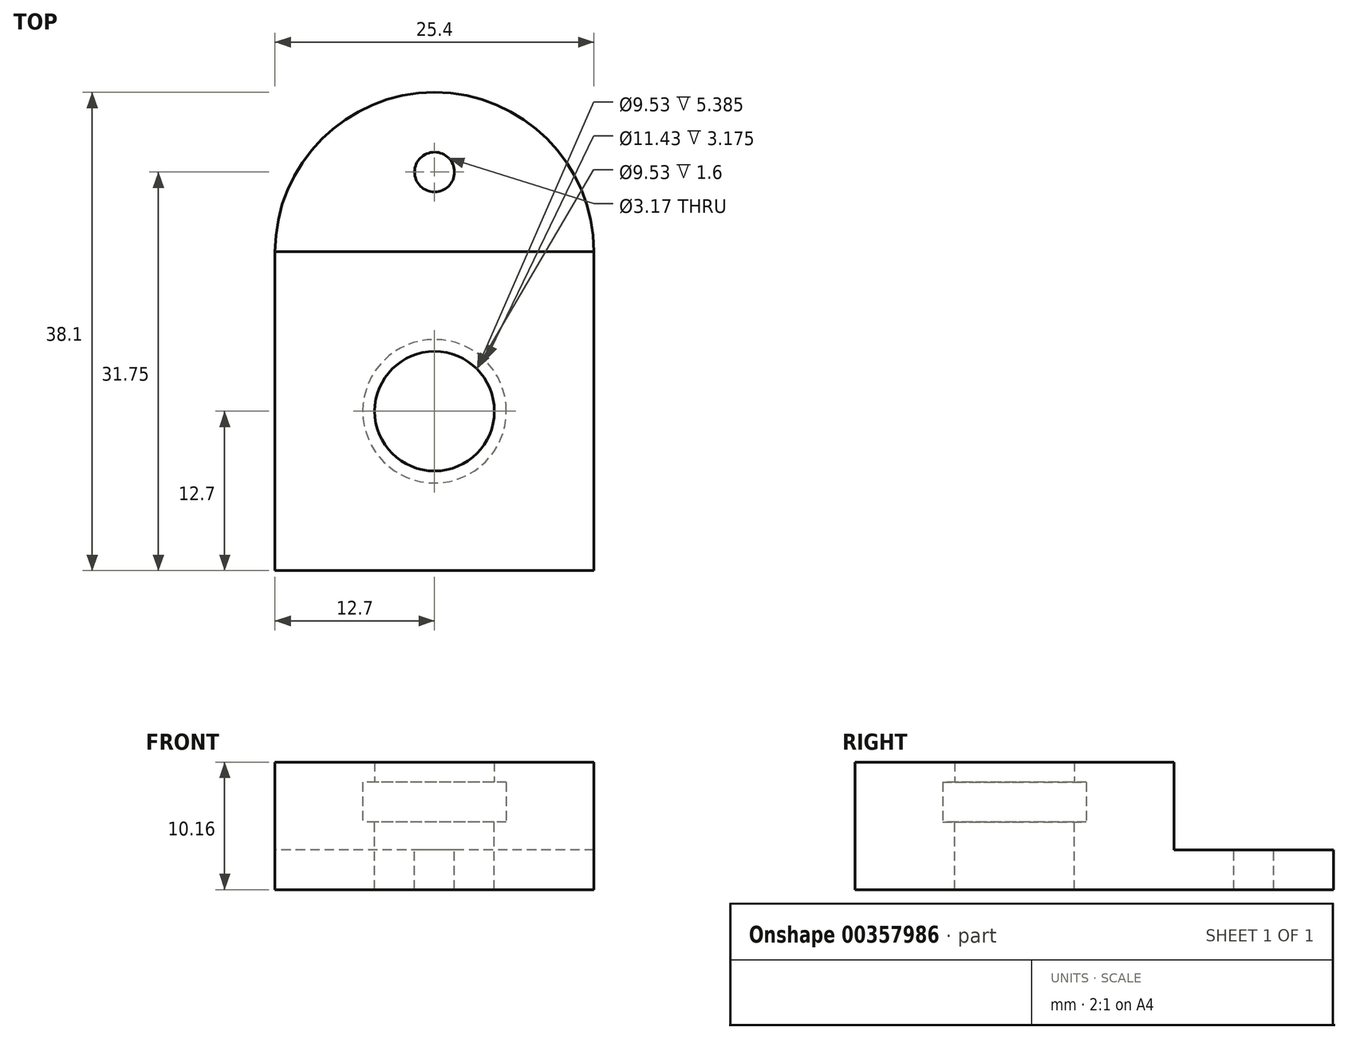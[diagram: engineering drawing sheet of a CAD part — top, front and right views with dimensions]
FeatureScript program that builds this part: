
annotation { "Feature Type Name" : "Feature", "Feature Type Description" : "" }
export const myFeature = defineFeature(function(context is Context, id is Id, definition is map)
    precondition{}
    {
        {
            var Q0;
            Q0=qCreatedBy(makeId("Top.planeOp"),FACE);
            var sketch = newSketch(context, id + "F0", { "sketchPlane" : qUnion([Q0])});
            skLineSegment(sketch, "E0.top", {"start": v(12.7, -12.7) * mm, "end": v(-12.7, -12.7) * mm});
            skLineSegment(sketch, "E0.left", {"start": v(12.7, 12.7) * mm, "end": v(12.7, -12.7) * mm});
            skLineSegment(sketch, "E0.right", {"start": v(-12.7, 12.7) * mm, "end": v(-12.7, -12.7) * mm});
            skPoint(sketch, "E0.middle", {"position": v(0, 0) * mm});
            skArc(sketch, "E1", {"start": v(-12.7, 12.7) * mm, "mid": v(0, 25.4) * mm, "end": v(12.7, 12.7) * mm});
            skSolve(sketch);
        }
        {
            var Q0;
            Q0=makeQuery(id+"F0.imprint","IMPRINT",FACE,{"disambiguationData":[TD([[makeQuery(id+"F0.imprint","IMPRINT",EDGE,{"derivedFrom":sQuery(id+"F0.wireOp",EDGE,"E0.top")}),-1.0]])]});
            extrude(context, id + "F1", {"entities" : qUnion([Q0]), "depth" : 3.17 * mm});
        }
        {
            var Q0;
            Q0=makeQuery(id+"F1.opExtrude","CAP_FACE",FACE,{"disambiguationData":[OSD([sQuery(id+"F0.wireOp",EDGE,"E0.top"),sQuery(id+"F0.wireOp",EDGE,"E0.left"),sQuery(id+"F0.wireOp",EDGE,"E0.right"),sQuery(id+"F0.wireOp",EDGE,"E1")])],"isStart":false});
            var sketch = newSketch(context, id + "F2", { "sketchPlane" : qUnion([Q0])});
            skLineSegment(sketch, "E2.bottom", {"start": v(12.7, 12.7) * mm, "end": v(-12.7, 12.7) * mm});
            skLineSegment(sketch, "E2.top", {"start": v(12.7, -12.7) * mm, "end": v(-12.7, -12.7) * mm});
            skLineSegment(sketch, "E2.left", {"start": v(12.7, 12.7) * mm, "end": v(12.7, -12.7) * mm});
            skLineSegment(sketch, "E2.right", {"start": v(-12.7, 12.7) * mm, "end": v(-12.7, -12.7) * mm});
            skPoint(sketch, "E2.middle", {"position": v(0, 0) * mm});
            skSolve(sketch);
        }
        {
            var Q0;
            Q0 = qSketchRegion(id + "F2", true);
            extrude(context, id + "F3", {"entities" : qUnion([Q0]), "operationType" : NewBodyOperationType.ADD, "depth" : 2.2 * mm});
        }
        {
            var Q0;
            Q0=makeQuery(id+"F3.opExtrude","CAP_FACE",FACE,{"disambiguationData":[OSD([sQuery(id+"F2.wireOp",EDGE,"E2.bottom"),sQuery(id+"F2.wireOp",EDGE,"E2.top"),sQuery(id+"F2.wireOp",EDGE,"E2.left"),sQuery(id+"F2.wireOp",EDGE,"E2.right")])],"isStart":false});
            var sketch = newSketch(context, id + "F4", { "sketchPlane" : qUnion([Q0])});
            skCircle(sketch, "E3", {"center": v(0, 0) * mm, "radius": 4.76 * mm});
            skSolve(sketch);
        }
        {
            var Q0;
            Q0=sQuery(id+"F4.wireOp",VERTEX,"E3.center");
            var Q1;
            Q1=makeQuery(id+"F1.opExtrude","SWEPT_BODY",BODY,{"disambiguationData":[OSD([sQuery(id+"F0.wireOp",EDGE,"E0.top"),sQuery(id+"F0.wireOp",EDGE,"E0.left"),sQuery(id+"F0.wireOp",EDGE,"E0.right"),sQuery(id+"F0.wireOp",EDGE,"E1")])]});
            hole(context, id + "F5", {"style" : HoleStyle.SIMPLE, "endStyle" : HoleEndStyle.THROUGH, "holeDiameter" : 9.52 * mm, "isTappedThrough" : true, "tappedDepth" : 12.7 * mm, "tapClearance" : 3, "locations" : qUnion([Q0]), "scope" : qUnion([Q1])});
        }
        {
            var Q0;
            Q0=makeQuery(id+"F3.opExtrude","CAP_FACE",FACE,{"disambiguationData":[OSD([sQuery(id+"F2.wireOp",EDGE,"E2.bottom"),sQuery(id+"F2.wireOp",EDGE,"E2.top"),sQuery(id+"F2.wireOp",EDGE,"E2.left"),sQuery(id+"F2.wireOp",EDGE,"E2.right")])],"isStart":false});
            var sketch = newSketch(context, id + "F6", { "sketchPlane" : qUnion([Q0])});
            skLineSegment(sketch, "E4.bottom", {"start": v(12.7, 12.7) * mm, "end": v(-12.7, 12.7) * mm});
            skLineSegment(sketch, "E4.top", {"start": v(12.7, -12.7) * mm, "end": v(-12.7, -12.7) * mm});
            skLineSegment(sketch, "E4.left", {"start": v(12.7, 12.7) * mm, "end": v(12.7, -12.7) * mm});
            skLineSegment(sketch, "E4.right", {"start": v(-12.7, 12.7) * mm, "end": v(-12.7, -12.7) * mm});
            skPoint(sketch, "E4.middle", {"position": v(0, 0) * mm});
            skCircle(sketch, "E5", {"center": v(0, 0) * mm, "radius": 5.72 * mm});
            skSolve(sketch);
        }
        {
            var Q0;
            Q0 = qSketchRegion(id + "F6", true);
            extrude(context, id + "F7", {"entities" : qUnion([Q0]), "operationType" : NewBodyOperationType.ADD, "depth" : 3.17 * mm});
        }
        {
            var Q0;
            Q0=makeQuery(id+"F7.opExtrude","CAP_FACE",FACE,{"disambiguationData":[OSD([sQuery(id+"F6.wireOp",EDGE,"E4.bottom"),sQuery(id+"F6.wireOp",EDGE,"E4.top"),sQuery(id+"F6.wireOp",EDGE,"E4.left"),sQuery(id+"F6.wireOp",EDGE,"E4.right"),sQuery(id+"F6.wireOp",EDGE,"E5")])],"isStart":false});
            var sketch = newSketch(context, id + "F8", { "sketchPlane" : qUnion([Q0])});
            skLineSegment(sketch, "E6.bottom", {"start": v(12.7, 12.7) * mm, "end": v(-12.7, 12.7) * mm});
            skLineSegment(sketch, "E6.top", {"start": v(12.7, -12.7) * mm, "end": v(-12.7, -12.7) * mm});
            skLineSegment(sketch, "E6.left", {"start": v(12.7, 12.7) * mm, "end": v(12.7, -12.7) * mm});
            skLineSegment(sketch, "E6.right", {"start": v(-12.7, 12.7) * mm, "end": v(-12.7, -12.7) * mm});
            skPoint(sketch, "E6.middle", {"position": v(0, 0) * mm});
            skCircle(sketch, "E7", {"center": v(0, 0) * mm, "radius": 4.76 * mm});
            skSolve(sketch);
        }
        {
            var Q0;
            Q0 = qSketchRegion(id + "F8", true);
            extrude(context, id + "F9", {"entities" : qUnion([Q0]), "operationType" : NewBodyOperationType.ADD, "depth" : 1.6 * mm});
        }
        {
            var Q0;
            Q0=makeQuery(id+"F1.opExtrude","CAP_FACE",FACE,{"disambiguationData":[OSD([sQuery(id+"F0.wireOp",EDGE,"E0.top"),sQuery(id+"F0.wireOp",EDGE,"E0.left"),sQuery(id+"F0.wireOp",EDGE,"E0.right"),sQuery(id+"F0.wireOp",EDGE,"E1")])],"isStart":false});
            var sketch = newSketch(context, id + "F10", { "sketchPlane" : qUnion([Q0])});
            skPoint(sketch, "E8", {"position": v(0, 19.05) * mm});
            skSolve(sketch);
        }
        {
            var Q0;
            Q0=sQuery(id+"F10.wireOp",VERTEX,"E8");
            var Q1;
            Q1=makeQuery(id+"F1.opExtrude","SWEPT_BODY",BODY,{"disambiguationData":[OSD([sQuery(id+"F0.wireOp",EDGE,"E0.top"),sQuery(id+"F0.wireOp",EDGE,"E0.left"),sQuery(id+"F0.wireOp",EDGE,"E0.right"),sQuery(id+"F0.wireOp",EDGE,"E1")])]});
            hole(context, id + "F11", {"style" : HoleStyle.SIMPLE, "endStyle" : HoleEndStyle.THROUGH, "holeDiameter" : 3.17 * mm, "isTappedThrough" : true, "tappedDepth" : 12.7 * mm, "tapClearance" : 3, "locations" : qUnion([Q0]), "scope" : qUnion([Q1])});
        }
    });
